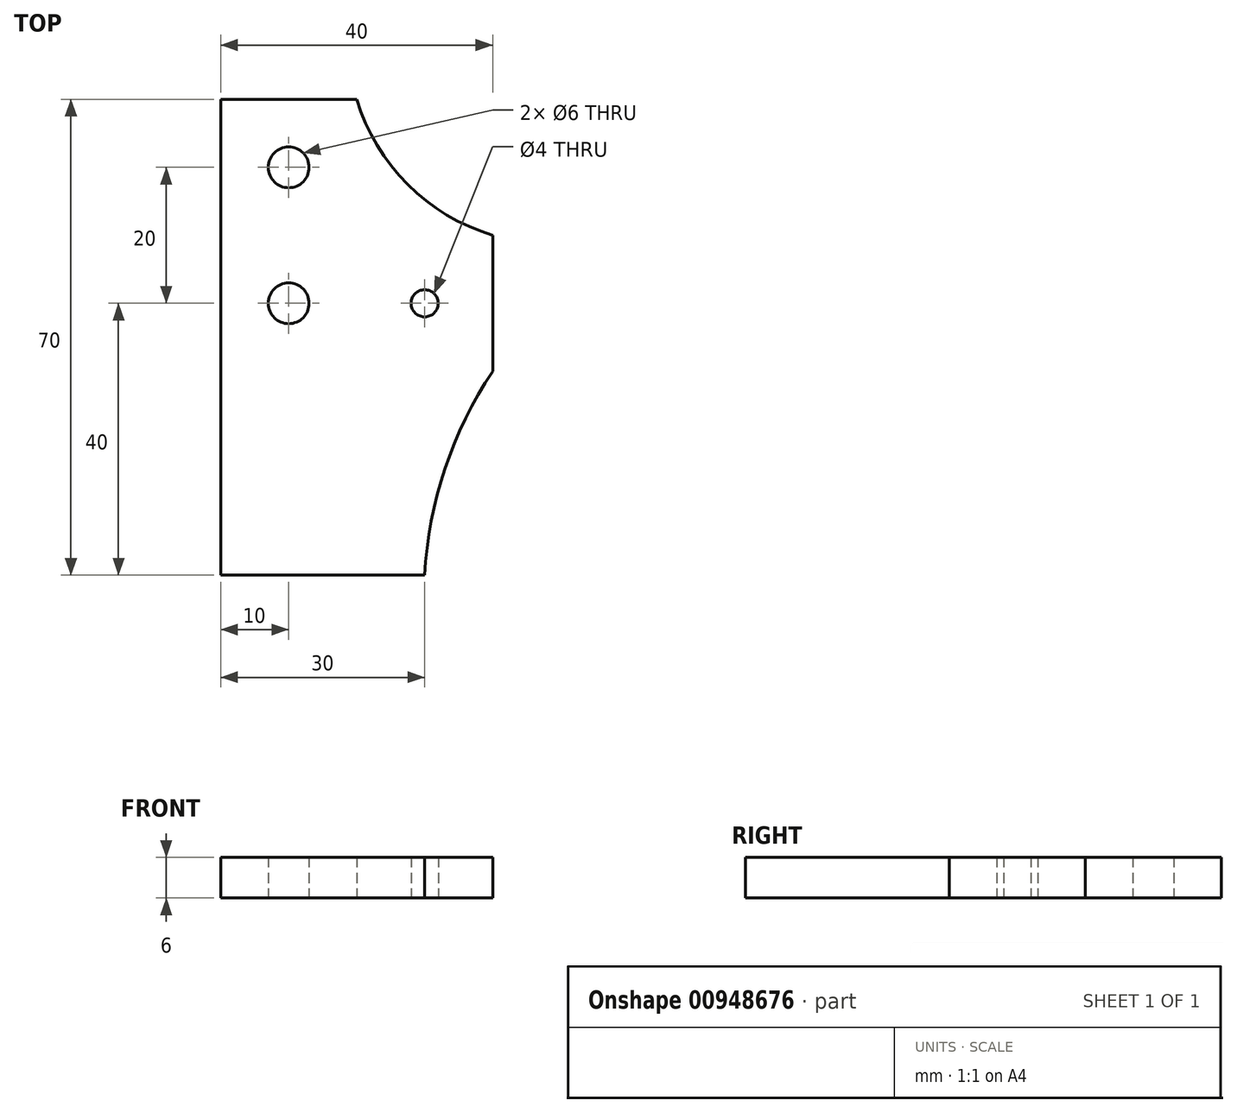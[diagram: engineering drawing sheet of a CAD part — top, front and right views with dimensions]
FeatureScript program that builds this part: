
annotation { "Feature Type Name" : "Feature", "Feature Type Description" : "" }
export const myFeature = defineFeature(function(context is Context, id is Id, definition is map)
    precondition{}
    {
        {
            var Q0;
            Q0=qCreatedBy(makeId("Top.planeOp"),FACE);
            var sketch = newSketch(context, id + "F0", { "sketchPlane" : qUnion([Q0])});
            skLineSegment(sketch, "E0", {"start": v(10, 10) * mm, "end": v(-10, 10) * mm});
            skLineSegment(sketch, "E1", {"start": v(-10, 10) * mm, "end": v(-10, -60) * mm});
            skLineSegment(sketch, "E2", {"start": v(-10, -60) * mm, "end": v(20, -60) * mm});
            skLineSegment(sketch, "E3", {"start": v(0, 22.52) * mm, "end": v(0, -45.28) * mm, "construction": true});
            skLineSegment(sketch, "E4", {"start": v(-27.65, 0) * mm, "end": v(25.7, 0) * mm, "construction": true});
            skLineSegment(sketch, "E5", {"start": v(-26.79, -20) * mm, "end": v(25.2, -20) * mm, "construction": true});
            skCircle(sketch, "E6", {"center": v(0, 0) * mm, "radius": 3 * mm});
            skCircle(sketch, "E7", {"center": v(0, -20) * mm, "radius": 3 * mm});
            skLineSegment(sketch, "E8", {"start": v(20, 21.66) * mm, "end": v(20, -46.13) * mm, "construction": true});
            skCircle(sketch, "E9", {"center": v(20, -20) * mm, "radius": 2 * mm});
            skLineSegment(sketch, "E10", {"start": v(30, -10) * mm, "end": v(30, -30) * mm});
            skArc(sketch, "E11", {"start": v(30, -30) * mm, "mid": v(22.99, -44.33) * mm, "end": v(20, -60) * mm});
            skArc(sketch, "E12", {"start": v(10, 10) * mm, "mid": v(17.5, -2.5) * mm, "end": v(30, -10) * mm});
            skSolve(sketch);
        }
        {
            var Q0;
            Q0=makeQuery(id+"F0.imprint","IMPRINT",FACE,{"disambiguationData":[TD([[makeQuery(id+"F0.imprint","IMPRINT",EDGE,{"derivedFrom":sQuery(id+"F0.wireOp",EDGE,"E0")}),1.0]])]});
            extrude(context, id + "F1", {"entities" : qUnion([Q0]), "depth" : 6 * mm, "offsetDistance" : 25 * mm});
        }
    });
